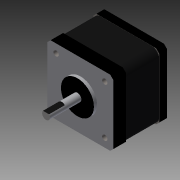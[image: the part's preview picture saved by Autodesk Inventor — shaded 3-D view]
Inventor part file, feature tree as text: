
AUTODESK INVENTOR PART (.ipt)
format: ipt  version: 2020 (Build 240168000, 168)  size: 185,856 bytes
history: native  units: in
note: dims shown in document units (in); Inventor stores cm internally (conversion verified against a paired STEP export)
features: extrude x3, sketch x3, other x2, imported_body x1
ambient origin geometry x8: Origin, YZ Plane, XZ Plane, XY Plane, X Axis, Y Axis, Z Axis, Center Point
bodies: Body1 (feature_tree)
feature tree (9):
  other  "Cut-Extrude6"
  other  "stepper (hardware)1"
  extrude  "Extrusion1"  Depth=0.1969in TaperAngle=0.0deg
  extrude  "Extrusion2"  [1 undecoded]
  extrude  "Extrusion3"  [1 undecoded]
  imported_body  "Base1"
  sketch  "Sketch2"  dims[d0=0.1969in d1=0.0in d2=0.1969in d3=0.0in]
  sketch  "Sketch3"  dims[d4=0.3937in d5=0.0in]
  sketch  "Sketch4"
note: 2 required parameter values undecoded (feature->parameter linkage not recoverable at this tier; creation-order binding heuristic only, values carry confidence <= 0.55)
